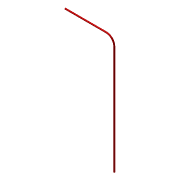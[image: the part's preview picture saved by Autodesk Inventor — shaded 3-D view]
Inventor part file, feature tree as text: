
AUTODESK INVENTOR PART (.ipt)
format: ipt  version: unknown  size: 166,912 bytes
history: native  units: in
note: dims shown in document units (in); Inventor stores cm internally (conversion verified against a paired STEP export)
features: sketch x2, sweep x1, other x1
ambient origin geometry x8: Origin, YZ Plane, XZ Plane, XY Plane, X Axis, Y Axis, Z Axis, Center Point
feature tree (4):
  sweep  "Sweep7"
  other  "Work Axis11"
  sketch  "Sketch21"  dims[d66=0.4724in d68=1.1811in]
  sketch  "Sketch22"  dims[d69=0.0394in d70=0.0in d72=3.1496in]
